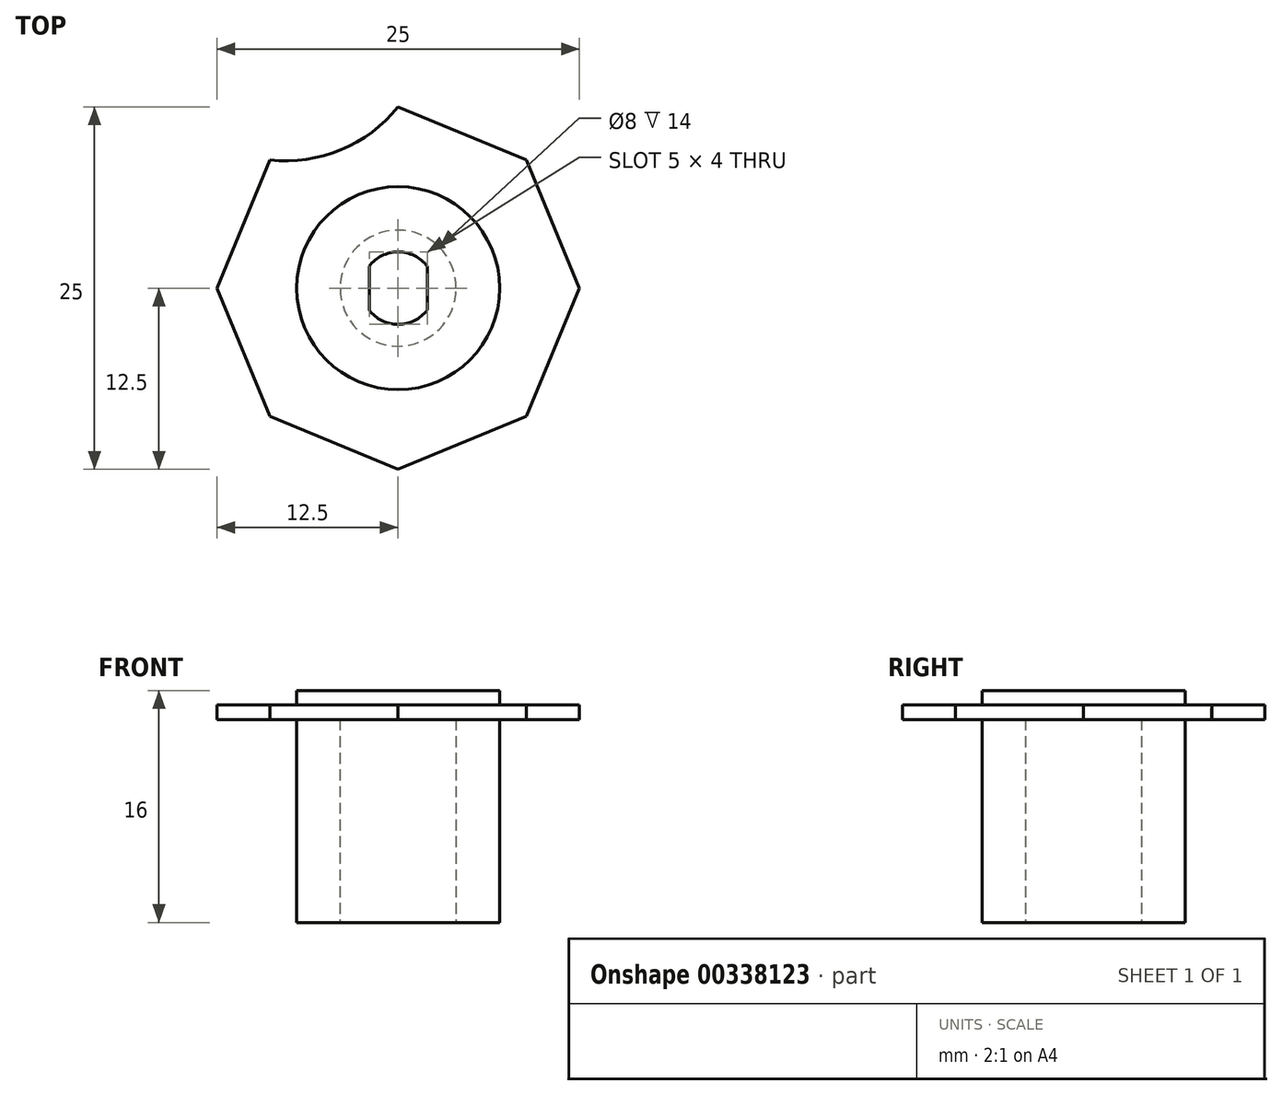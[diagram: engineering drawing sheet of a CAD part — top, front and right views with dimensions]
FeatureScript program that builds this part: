
annotation { "Feature Type Name" : "Feature", "Feature Type Description" : "" }
export const myFeature = defineFeature(function(context is Context, id is Id, definition is map)
    precondition{}
    {
        {
            var Q0;
            Q0=qCreatedBy(makeId("Top.planeOp"),FACE);
            var sketch = newSketch(context, id + "F0", { "sketchPlane" : qUnion([Q0])});
            skCircle(sketch, "E0", {"center": v(0, 0) * mm, "radius": 7 * mm});
            skSolve(sketch);
        }
        {
            var Q0;
            Q0 = qSketchRegion(id + "F0", true);
            extrude(context, id + "F1", {"entities" : qUnion([Q0]), "depth" : 16 * mm});
        }
        {
            var Q0;
            Q0=makeQuery(id+"F1.opExtrude","CAP_FACE",FACE,{"disambiguationData":[OSD([sQuery(id+"F0.wireOp",EDGE,"E0")])],"isStart":false});
            cPlane(context, id + "F2", {"entities" : qUnion([Q0]), "cplaneType" : CPlaneType.OFFSET, "offset" : 1 * mm, "oppositeDirection" : true, "width" : 150 * mm, "height" : 150 * mm});
        }
        {
            var Q0;
            Q0=qCreatedBy(id+"F2.planeOp",FACE);
            var sketch = newSketch(context, id + "F3", { "sketchPlane" : qUnion([Q0])});
            skCircle(sketch, "E1.cCircle", {"center": v(0, 0) * mm, "radius": 12.5 * mm, "construction": true});
            skLineSegment(sketch, "E1.0", {"start": v(0, 12.5) * mm, "end": v(8.84, 8.84) * mm});
            skLineSegment(sketch, "E1.1", {"start": v(8.84, 8.84) * mm, "end": v(12.5, 0) * mm});
            skLineSegment(sketch, "E1.2", {"start": v(12.5, 0) * mm, "end": v(8.84, -8.84) * mm});
            skLineSegment(sketch, "E1.3", {"start": v(8.84, -8.84) * mm, "end": v(0, -12.5) * mm});
            skLineSegment(sketch, "E1.4", {"start": v(0, -12.5) * mm, "end": v(-8.84, -8.84) * mm});
            skLineSegment(sketch, "E1.5", {"start": v(-8.84, -8.84) * mm, "end": v(-12.5, 0) * mm});
            skLineSegment(sketch, "E1.6", {"start": v(-12.5, 0) * mm, "end": v(-8.84, 8.84) * mm});
            skLineSegment(sketch, "E1.7", {"start": v(-8.84, 8.84) * mm, "end": v(0, 12.5) * mm});
            skSolve(sketch);
        }
        {
            var Q0;
            Q0 = qSketchRegion(id + "F3", true);
            extrude(context, id + "F4", {"entities" : qUnion([Q0]), "operationType" : NewBodyOperationType.ADD, "oppositeDirection" : true, "depth" : 1 * mm});
        }
        {
            var Q0;
            Q0=qCreatedBy(makeId("Top.planeOp"),FACE);
            var sketch = newSketch(context, id + "F5", { "sketchPlane" : qUnion([Q0])});
            skCircle(sketch, "E2", {"center": v(0, 0) * mm, "radius": 4 * mm});
            skSolve(sketch);
        }
        {
            var Q0;
            Q0 = qSketchRegion(id + "F5", true);
            var Q1;
            Q1=makeQuery(id+"F4.opExtrude","CAP_FACE",FACE,{"disambiguationData":[OSD([sQuery(id+"F3.wireOp",EDGE,"E1.0"),sQuery(id+"F3.wireOp",EDGE,"E1.1"),sQuery(id+"F3.wireOp",EDGE,"E1.2"),sQuery(id+"F3.wireOp",EDGE,"E1.3"),sQuery(id+"F3.wireOp",EDGE,"E1.4"),sQuery(id+"F3.wireOp",EDGE,"E1.5"),sQuery(id+"F3.wireOp",EDGE,"E1.6"),sQuery(id+"F3.wireOp",EDGE,"E1.7")])],"isStart":false});
            extrude(context, id + "F6", {"entities" : qUnion([Q0]), "operationType" : NewBodyOperationType.REMOVE, "endBound" : BoundingType.UP_TO_SURFACE, "endBoundEntityFace" : qUnion([Q1]), "depth" : 25 * mm});
        }
        {
            var Q0;
            Q0=makeQuery(id+"F1.opExtrude","CAP_FACE",FACE,{"disambiguationData":[OSD([sQuery(id+"F0.wireOp",EDGE,"E0")])],"isStart":false});
            var sketch = newSketch(context, id + "F7", { "sketchPlane" : qUnion([Q0])});
            skArc(sketch, "E3", {"start": v(-2, -1.5) * mm, "mid": v(0, -2.5) * mm, "end": v(2, -1.5) * mm});
            skLineSegment(sketch, "E4", {"start": v(-2, -1.5) * mm, "end": v(-2, 1.5) * mm});
            skLineSegment(sketch, "E5", {"start": v(2, -1.5) * mm, "end": v(2, 1.5) * mm});
            skArc(sketch, "E6.trimOffspring", {"start": v(2, 1.5) * mm, "mid": v(0, 2.5) * mm, "end": v(-2, 1.5) * mm});
            skSolve(sketch);
        }
        {
            var Q0;
            Q0 = qSketchRegion(id + "F7", true);
            extrude(context, id + "F8", {"entities" : qUnion([Q0]), "operationType" : NewBodyOperationType.REMOVE, "endBound" : BoundingType.THROUGH_ALL, "oppositeDirection" : true, "depth" : 25 * mm});
        }
        {
            var Q0;
            Q0=makeQuery(id+"F4.opExtrude","CAP_FACE",FACE,{"disambiguationData":[OSD([sQuery(id+"F3.wireOp",EDGE,"E1.0"),sQuery(id+"F3.wireOp",EDGE,"E1.1"),sQuery(id+"F3.wireOp",EDGE,"E1.2"),sQuery(id+"F3.wireOp",EDGE,"E1.3"),sQuery(id+"F3.wireOp",EDGE,"E1.4"),sQuery(id+"F3.wireOp",EDGE,"E1.5"),sQuery(id+"F3.wireOp",EDGE,"E1.6"),sQuery(id+"F3.wireOp",EDGE,"E1.7")])],"isStart":true});
            var sketch = newSketch(context, id + "F9", { "sketchPlane" : qUnion([Q0])});
            skArc(sketch, "E7", {"start": v(-8.84, 8.84) * mm, "mid": v(-3.95, 9.54) * mm, "end": v(0, 12.5) * mm});
            skLineSegment(sketch, "E8", {"start": v(-8.84, 8.84) * mm, "end": v(0, 12.5) * mm});
            skSolve(sketch);
        }
        {
            var Q0;
            Q0 = qSketchRegion(id + "F9", true);
            extrude(context, id + "F10", {"entities" : qUnion([Q0]), "endBound" : BoundingType.THROUGH_ALL, "oppositeDirection" : true, "depth" : 25 * mm});
        }
        {
            var Q0;
            Q0=makeQuery(id+"F10.opExtrude","CAP_FACE",FACE,{"disambiguationData":[OSD([sQuery(id+"F9.wireOp",EDGE,"E7"),sQuery(id+"F9.wireOp",EDGE,"E8")])],"isStart":true});
            var sketch = newSketch(context, id + "F11", { "sketchPlane" : qUnion([Q0])});
            skLineSegment(sketch, "E9", {"start": v(0, 12.5) * mm, "end": v(-8.84, 8.84) * mm});
            skArc(sketch, "E10.0", {"start": v(-8.84, 8.84) * mm, "mid": v(-3.95, 9.54) * mm, "end": v(0, 12.5) * mm});
            skSolve(sketch);
        }
        {
            var Q0;
            Q0 = qSketchRegion(id + "F11", true);
            extrude(context, id + "F12", {"entities" : qUnion([Q0]), "operationType" : NewBodyOperationType.REMOVE, "endBound" : BoundingType.THROUGH_ALL, "oppositeDirection" : true, "depth" : 25 * mm});
        }
    });
